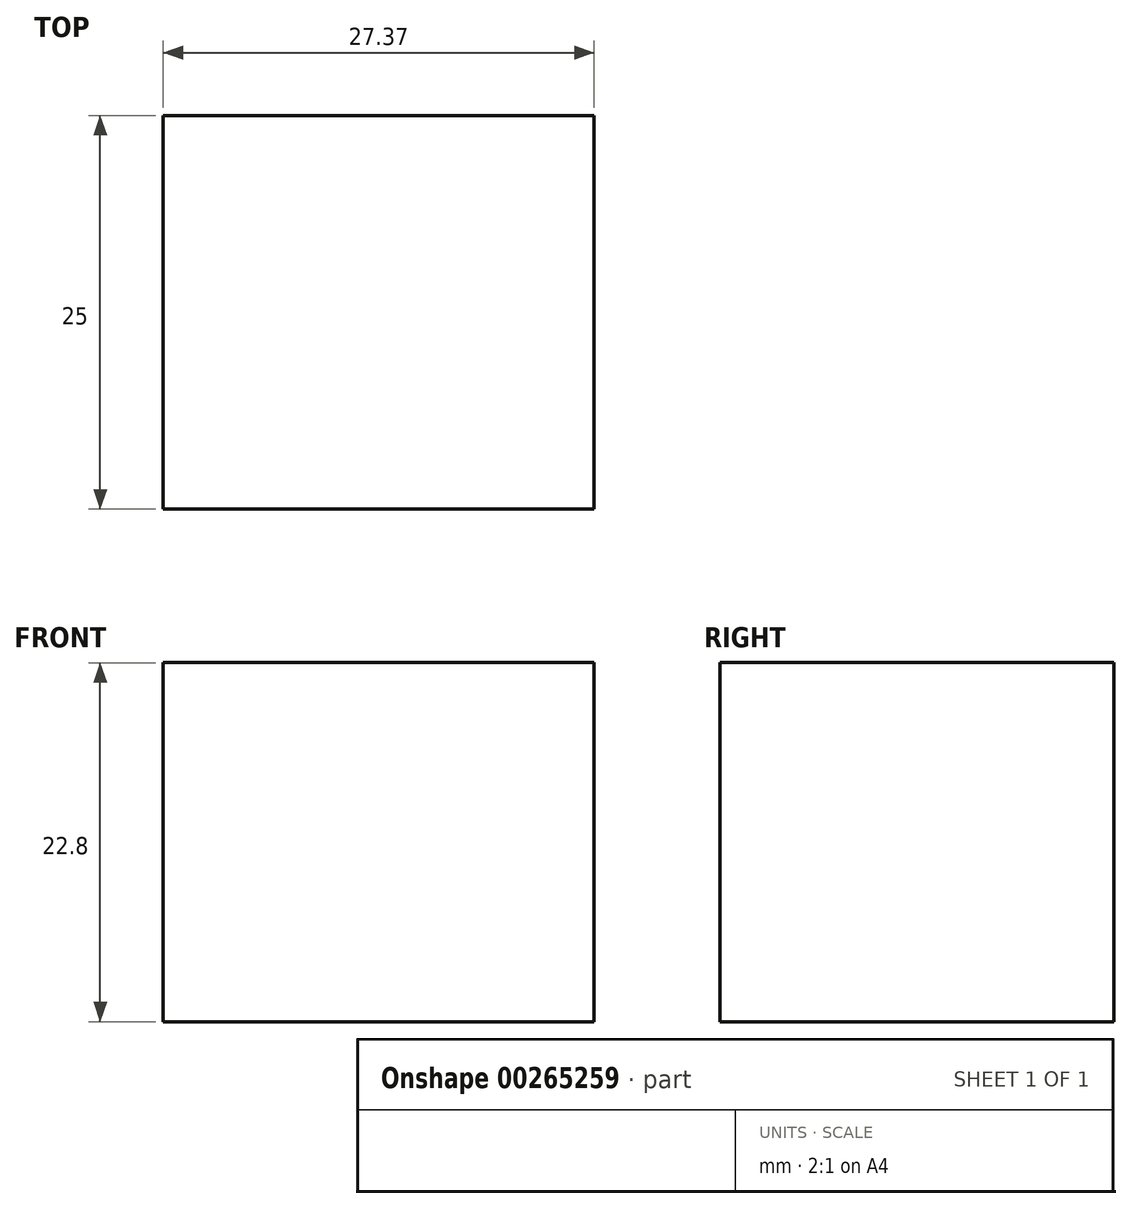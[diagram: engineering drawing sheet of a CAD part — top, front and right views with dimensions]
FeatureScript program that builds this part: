
annotation { "Feature Type Name" : "Feature", "Feature Type Description" : "" }
export const myFeature = defineFeature(function(context is Context, id is Id, definition is map)
    precondition{}
    {
        {
            var Q0;
            Q0=qCreatedBy(makeId("Front.planeOp"),FACE);
            var sketch = newSketch(context, id + "F0", { "sketchPlane" : qUnion([Q0])});
            skLineSegment(sketch, "E0.bottom", {"start": v(-44.4, 64.62) * mm, "end": v(-17.02, 64.62) * mm});
            skLineSegment(sketch, "E0.top", {"start": v(-44.4, 41.82) * mm, "end": v(-17.02, 41.82) * mm});
            skLineSegment(sketch, "E0.left", {"start": v(-44.4, 64.62) * mm, "end": v(-44.4, 41.82) * mm});
            skLineSegment(sketch, "E0.right", {"start": v(-17.02, 64.62) * mm, "end": v(-17.02, 41.82) * mm});
            skSolve(sketch);
        }
        {
            var Q0;
            Q0 = qSketchRegion(id + "F0", true);
            extrude(context, id + "F1", {"entities" : qUnion([Q0]), "depth" : 25 * mm});
        }
    });
